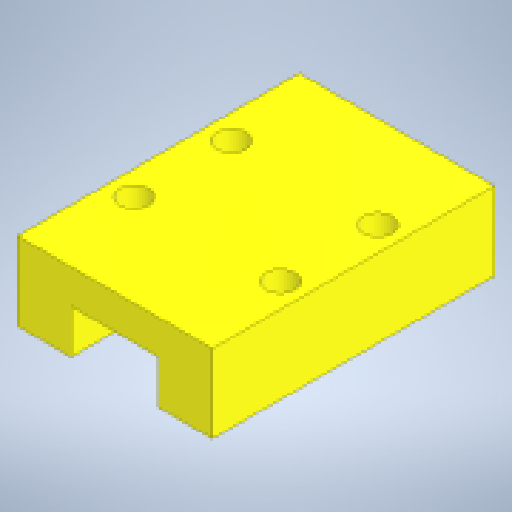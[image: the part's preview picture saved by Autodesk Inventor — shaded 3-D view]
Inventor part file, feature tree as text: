
AUTODESK INVENTOR PART (.ipt)
format: ipt  version: 2024.1 (Build 281209000, 209)  size: 158,208 bytes
history: native  units: in
note: dims shown in document units (in); Inventor stores cm internally (conversion verified against a paired STEP export)
features: extrude x2, sketch x2
ambient origin geometry x8: Origin, YZ Plane, XZ Plane, XY Plane, X Axis, Y Axis, Z Axis, Center Point
bodies: Solid1 (feature_tree)
feature tree (4):
  extrude  "Extrusion1"  Depth=0.315in
  extrude  "Extrusion2"  Depth=0.3543in
  sketch  "Sketch1"  dims[d0=0.7874in d1=0.315in]
  sketch  "Sketch2"  dims[d2=0.1772in d3=0.3543in d4=0.2165in d5=1.1378in d6=0.0in d7=0.1181in d8=0.1181in d9=0.1181in d10=0.1181in d11=0.372in d12=0.372in d13=0.3937in d14=0.3937in d15=0.0984in d16=0.0984in d18=0.0984in d19=0.0984in d20=0.315in d21=0.0in]
